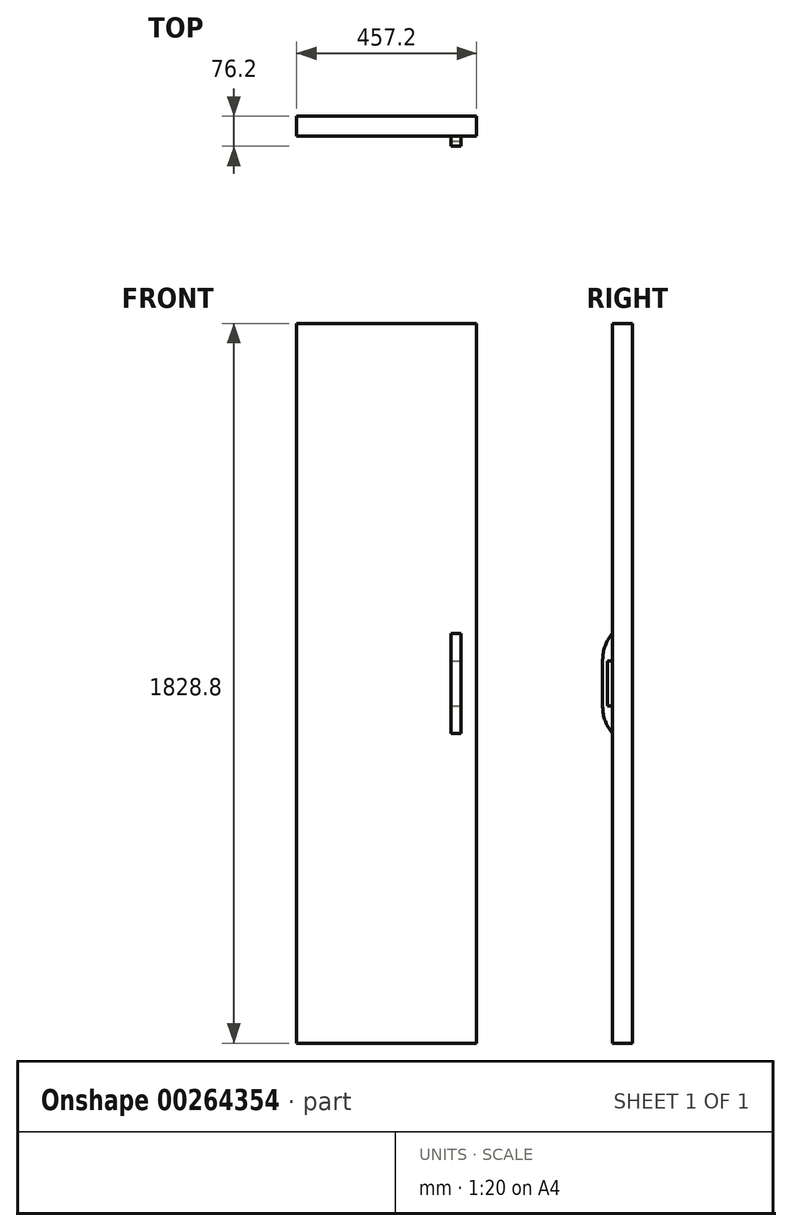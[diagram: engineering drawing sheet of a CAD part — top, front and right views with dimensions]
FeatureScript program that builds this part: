
annotation { "Feature Type Name" : "Feature", "Feature Type Description" : "" }
export const myFeature = defineFeature(function(context is Context, id is Id, definition is map)
    precondition{}
    {
        {
            var Q0;
            Q0=qCreatedBy(makeId("Front.planeOp"),FACE);
            var sketch = newSketch(context, id + "F0", { "sketchPlane" : qUnion([Q0])});
            skLineSegment(sketch, "E0.bottom", {"start": v(-228.6, 914.4) * mm, "end": v(228.6, 914.4) * mm});
            skLineSegment(sketch, "E0.top", {"start": v(-228.6, -914.4) * mm, "end": v(228.6, -914.4) * mm});
            skLineSegment(sketch, "E0.left", {"start": v(-228.6, 914.4) * mm, "end": v(-228.6, -914.4) * mm});
            skLineSegment(sketch, "E0.right", {"start": v(228.6, 914.4) * mm, "end": v(228.6, -914.4) * mm});
            skPoint(sketch, "E0.middle", {"position": v(0, 0) * mm});
            skSolve(sketch);
        }
        {
            var Q0;
            Q0=makeQuery(id+"F0.imprint","IMPRINT",FACE,{"disambiguationData":[TD([[makeQuery(id+"F0.imprint","IMPRINT",EDGE,{"derivedFrom":sQuery(id+"F0.wireOp",EDGE,"E0.bottom")}),-1.0]])]});
            extrude(context, id + "F1", {"entities" : qUnion([Q0]), "depth" : 50.8 * mm});
        }
        {
            var Q0;
            Q0=makeQuery(id+"F1.opExtrude","CAP_FACE",FACE,{"disambiguationData":[OSD([sQuery(id+"F0.wireOp",EDGE,"E0.bottom"),sQuery(id+"F0.wireOp",EDGE,"E0.top"),sQuery(id+"F0.wireOp",EDGE,"E0.left"),sQuery(id+"F0.wireOp",EDGE,"E0.right")])],"isStart":false});
            var sketch = newSketch(context, id + "F2", { "sketchPlane" : qUnion([Q0])});
            skLineSegment(sketch, "E1.bottom", {"start": v(188.67, 127) * mm, "end": v(163.27, 127) * mm});
            skLineSegment(sketch, "E1.top", {"start": v(188.67, -127) * mm, "end": v(163.27, -127) * mm});
            skLineSegment(sketch, "E1.left", {"start": v(188.67, 127) * mm, "end": v(188.67, -127) * mm});
            skLineSegment(sketch, "E1.right", {"start": v(163.27, 127) * mm, "end": v(163.27, -127) * mm});
            skPoint(sketch, "E1.middle", {"position": v(175.97, 0) * mm});
            skSolve(sketch);
        }
        {
            var Q0;
            Q0=makeQuery(id+"F2.imprint","IMPRINT",FACE,{"disambiguationData":[TD([[makeQuery(id+"F2.imprint","IMPRINT",EDGE,{"derivedFrom":sQuery(id+"F2.wireOp",EDGE,"E1.bottom")}),1.0]])]});
            extrude(context, id + "F3", {"entities" : qUnion([Q0]), "operationType" : NewBodyOperationType.ADD, "depth" : 25.4 * mm});
        }
        {
            var Q0;
            Q0=makeQuery(id+"F3.opExtrude","CAP_EDGE",EDGE,{"disambiguationData":[OSD([sQuery(id+"F2.wireOp",EDGE,"E1.bottom")])],"isStart":false});
            var Q1;
            Q1=makeQuery(id+"F3.opExtrude","CAP_EDGE",EDGE,{"disambiguationData":[OSD([sQuery(id+"F2.wireOp",EDGE,"E1.top")])],"isStart":false});
            fillet(context, id + "F4", {"entities" : qUnion([Q0, Q1]), "radius" : 101.6 * mm, "tangentPropagation" : true, "allowEdgeOverflow" : false});
        }
        {
            var Q0;
            Q0=makeQuery(id+"F3.opExtrude","SWEPT_FACE",FACE,{"disambiguationData":[OSD([sQuery(id+"F2.wireOp",EDGE,"E1.left")])]});
            var sketch = newSketch(context, id + "F5", { "sketchPlane" : qUnion([Q0])});
            skLineSegment(sketch, "E2.bottom", {"start": v(-50.8, 0) * mm, "end": v(-63.5, 0) * mm});
            skLineSegment(sketch, "E2.top", {"start": v(-50.8, 57.15) * mm, "end": v(-63.5, 57.15) * mm});
            skLineSegment(sketch, "E2.left", {"start": v(-50.8, 0) * mm, "end": v(-50.8, 57.15) * mm});
            skLineSegment(sketch, "E2.right", {"start": v(-63.5, 0) * mm, "end": v(-63.5, 57.15) * mm});
            skLineSegment(sketch, "E3.MirrorCS", {"start": v(-63.5, 0) * mm, "end": v(-63.5, -57.15) * mm});
            skLineSegment(sketch, "E4.bottom", {"start": v(-63.5, -57.15) * mm, "end": v(-50.8, -57.15) * mm});
            skLineSegment(sketch, "E4.top", {"start": v(-63.5, 0) * mm, "end": v(-50.8, 0) * mm});
            skLineSegment(sketch, "E4.left", {"start": v(-63.5, -57.15) * mm, "end": v(-63.5, 0) * mm});
            skLineSegment(sketch, "E4.right", {"start": v(-50.8, -57.15) * mm, "end": v(-50.8, 0) * mm});
            skSolve(sketch);
        }
        {
            var Q0;
            Q0=makeQuery(id+"F5.imprint","IMPRINT",FACE,{"disambiguationData":[TD([[makeQuery(id+"F5.imprint","IMPRINT",EDGE,{"derivedFrom":sQuery(id+"F5.wireOp",EDGE,"E4.bottom")}),1.0]])]});
            var Q1;
            Q1=makeQuery(id+"F5.imprint","IMPRINT",FACE,{"disambiguationData":[TD([[makeQuery(id+"F5.imprint","IMPRINT",EDGE,{"derivedFrom":sQuery(id+"F5.wireOp",EDGE,"E2.top")}),1.0]])]});
            extrude(context, id + "F6", {"entities" : qUnion([Q0, Q1]), "operationType" : NewBodyOperationType.REMOVE, "endBound" : BoundingType.THROUGH_ALL, "oppositeDirection" : true, "depth" : 25.4 * mm});
        }
    });
